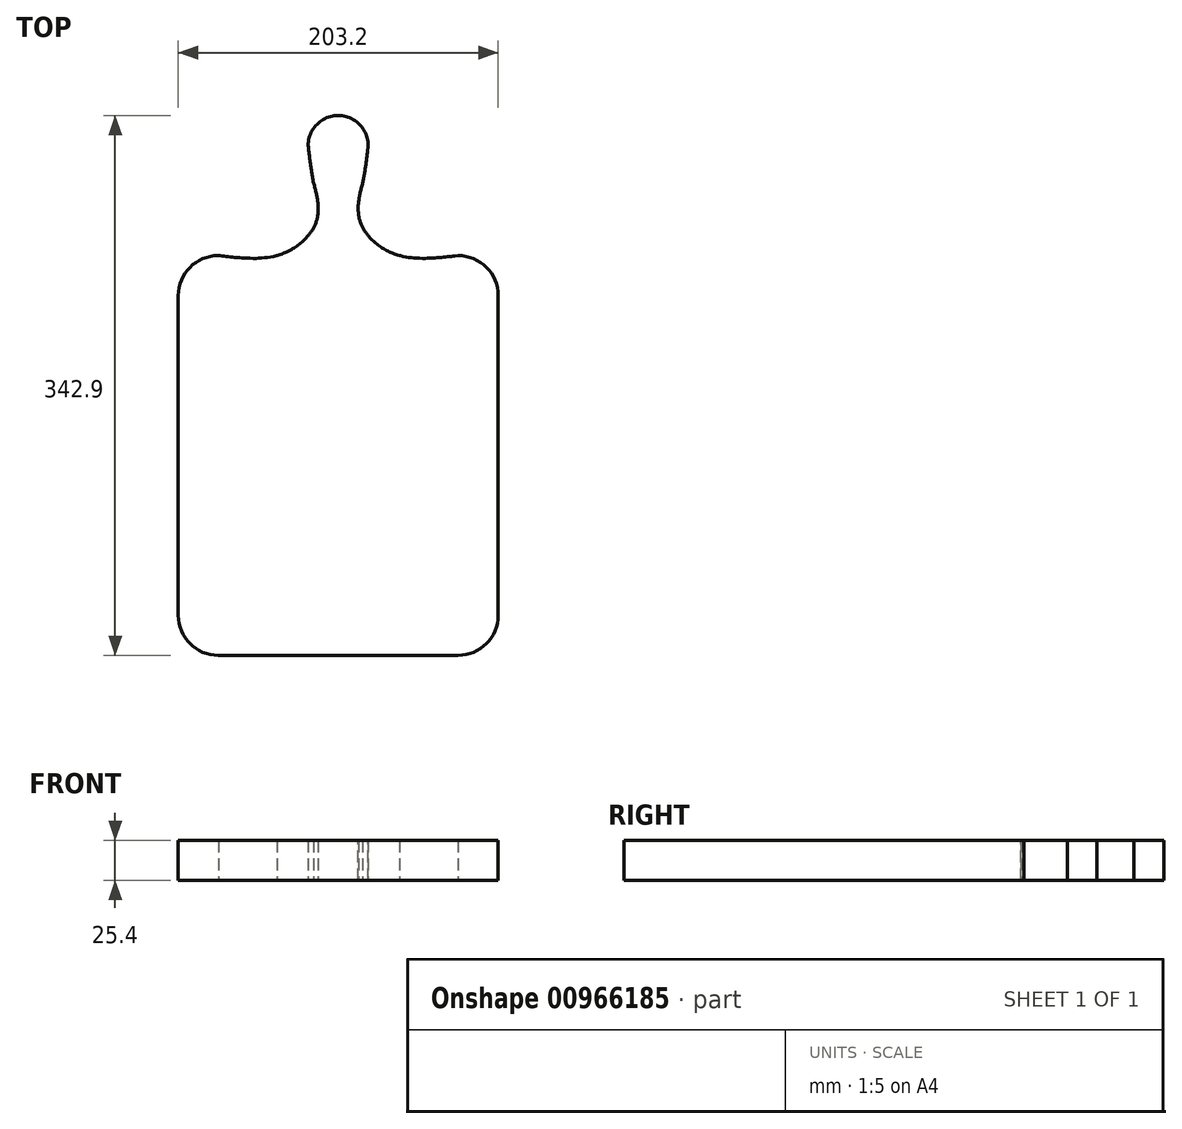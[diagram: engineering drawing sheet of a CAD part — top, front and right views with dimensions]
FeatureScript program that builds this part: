
annotation { "Feature Type Name" : "Feature", "Feature Type Description" : "" }
export const myFeature = defineFeature(function(context is Context, id is Id, definition is map)
    precondition{}
    {
        {
            var Q0;
            Q0=qCreatedBy(makeId("Top.planeOp"),FACE);
            var sketch = newSketch(context, id + "F0", { "sketchPlane" : qUnion([Q0])});
            skPoint(sketch, "E0", {"position": v(0, 88.78) * mm});
            skPoint(sketch, "E1", {"position": v(-19.05, 88.78) * mm});
            skPoint(sketch, "E2", {"position": v(-19.05, 0) * mm});
            skPoint(sketch, "E3", {"position": v(-101.6, 0) * mm});
            skPoint(sketch, "E4", {"position": v(-101.6, -254) * mm});
            skPoint(sketch, "E5", {"position": v(0, -254) * mm});
            skLineSegment(sketch, "E6", {"start": v(-41.9, 0) * mm, "end": v(-38.96, 0) * mm});
            skLineSegment(sketch, "E7", {"start": v(-101.6, -25.58) * mm, "end": v(-101.6, -228.53) * mm});
            skLineSegment(sketch, "E8", {"start": v(-76.17, -254) * mm, "end": v(0, -254) * mm});
            skLineSegment(sketch, "E9.MirrorCS", {"start": v(101.6, -25.58) * mm, "end": v(101.6, -228.53) * mm});
            skLineSegment(sketch, "E10.MirrorCS", {"start": v(76.17, -254) * mm, "end": v(0, -254) * mm});
            skPoint(sketch, "E11.1.internal.snap0", {"position": v(-19.05, 6.31) * mm});
            skFitSpline(sketch, "E12.MirrorCS", {"points": [v(19.05, 57.03) * mm, v(12.8, 27.54) * mm, v(19.05, 12.63) * mm], "startDerivative": vector(-18.2, -55.65) * mm, "endDerivative": vector(20.18, -31.93) * mm});
            skFitSpline(sketch, "E13.MirrorCS", {"points": [v(12.8, 27.54) * mm, v(19.05, 12.63) * mm, v(38.96, 0) * mm], "startDerivative": vector(8.67, -35.15) * mm, "endDerivative": vector(42.58, -20.4) * mm});
            skPoint(sketch, "E14.MirrorCS.start.orphan", {"position": v(30.48, 0) * mm});
            skArc(sketch, "E15", {"start": v(-76.1, 0) * mm, "mid": v(-94.14, -7.52) * mm, "end": v(-101.6, -25.58) * mm});
            skArc(sketch, "E16.MirrorCS", {"start": v(76.1, 0) * mm, "mid": v(94.14, -7.52) * mm, "end": v(101.6, -25.58) * mm});
            skArc(sketch, "E17", {"start": v(-101.6, -228.53) * mm, "mid": v(-94.13, -246.55) * mm, "end": v(-76.1, -254) * mm});
            skPoint(sketch, "E18.orphan", {"position": v(101.6, -0.28) * mm});
            skPoint(sketch, "E19.orphan", {"position": v(101.6, 0) * mm});
            skArc(sketch, "E20.MirrorCS", {"start": v(101.6, -228.53) * mm, "mid": v(94.13, -246.55) * mm, "end": v(76.1, -254) * mm});
            skPoint(sketch, "E21.orphan", {"position": v(101.6, -254) * mm});
            skPoint(sketch, "E22.orphan", {"position": v(-19.05, 44.4) * mm});
            skFitSpline(sketch, "E23.trimOffspring", {"points": [v(19.05, 57.03) * mm, v(15.62, 46.12) * mm, v(12.8, 27.54) * mm, v(19.05, 12.63) * mm, v(38.96, 0) * mm, v(76.1, 0) * mm], "startDerivative": vector(-22.47, -66.8) * mm, "endDerivative": vector(147.8, 15.82) * mm});
            skPoint(sketch, "E24.end.orphan", {"position": v(-38.96, 0) * mm});
            skPoint(sketch, "E25.2.internal.orphan", {"position": v(-19.05, 12.63) * mm});
            skFitSpline(sketch, "E26.MirrorCS", {"points": [v(-19.05, 57.03) * mm, v(-15.62, 46.12) * mm, v(-12.8, 27.54) * mm, v(-19.05, 12.63) * mm, v(-38.96, 0) * mm, v(-76.1, 0) * mm], "startDerivative": vector(22.47, -66.8) * mm, "endDerivative": vector(-147.8, 15.82) * mm});
            skPoint(sketch, "E27.orphan", {"position": v(19.05, 0) * mm});
            skPoint(sketch, "E28.end.orphan", {"position": v(-30.48, 0) * mm});
            skLineSegment(sketch, "E29", {"start": v(-39.18, -0.06) * mm, "end": v(-39.17, -0.06) * mm});
            skLineSegment(sketch, "E30", {"start": v(0, 0) * mm, "end": v(0, 69.85) * mm});
            skArc(sketch, "E31", {"start": v(18.52, 65.4) * mm, "mid": v(2.22, 88.77) * mm, "end": v(-19.05, 69.82) * mm});
            skFitSpline(sketch, "E32", {"points": [v(19.05, 69.82) * mm, v(15.62, 46.12) * mm, v(12.8, 27.54) * mm, v(19.05, 12.63) * mm, v(38.96, 0) * mm, v(62.87, -1.42) * mm, v(76.1, 0) * mm], "startDerivative": vector(-15.62, -132.33) * mm, "endDerivative": vector(88.56, 11.16) * mm});
            skFitSpline(sketch, "E33.trimOffspring", {"points": [v(19.05, 69.82) * mm, v(15.62, 46.12) * mm, v(12.8, 27.54) * mm, v(19.05, 12.63) * mm, v(38.96, 0) * mm, v(62.87, -1.42) * mm, v(76.1, 0) * mm], "startDerivative": vector(-15.62, -132.33) * mm, "endDerivative": vector(88.56, 11.16) * mm});
            skFitSpline(sketch, "E34.MirrorCS", {"points": [v(-19.05, 69.82) * mm, v(-15.62, 46.12) * mm, v(-12.8, 27.54) * mm, v(-19.05, 12.63) * mm, v(-38.96, 0) * mm, v(-62.87, -1.42) * mm, v(-76.1, 0) * mm], "startDerivative": vector(15.62, -132.33) * mm, "endDerivative": vector(-88.56, 11.16) * mm});
            skFitSpline(sketch, "E35.MirrorCS", {"points": [v(-19.05, 57.03) * mm, v(-12.8, 27.54) * mm, v(-19.05, 12.63) * mm], "startDerivative": vector(18.2, -55.65) * mm, "endDerivative": vector(-20.18, -31.93) * mm});
            skFitSpline(sketch, "E36.MirrorCS", {"points": [v(-19.05, 69.82) * mm, v(-15.62, 46.12) * mm, v(-12.8, 27.54) * mm, v(-19.05, 12.63) * mm, v(-38.96, 0) * mm, v(-62.87, -1.42) * mm, v(-76.1, 0) * mm], "startDerivative": vector(15.62, -132.33) * mm, "endDerivative": vector(-88.56, 11.16) * mm});
            skLineSegment(sketch, "E37.trimOffspring", {"start": v(39.63, -0.18) * mm, "end": v(39.67, -0.18) * mm});
            skLineSegment(sketch, "E38.trimOffspring", {"start": v(73.9, -0.24) * mm, "end": v(74.22, -0.24) * mm});
            skSolve(sketch);
        }
        {
            var Q0;
            {var subQ7=sQuery(id+"F0.wireOp",EDGE,"E7");Q0=makeQuery(id+"F0.imprint","IMPRINT",FACE,{"disambiguationData":[TD([[makeQuery(id+"F0.imprint","IMPRINT",EDGE,{"derivedFrom":subQ7}),1.0]])]});}
            extrude(context, id + "F1", {"entities" : qUnion([Q0]), "depth" : 25.4 * mm, "offsetDistance" : 25.4 * mm});
        }
    });
